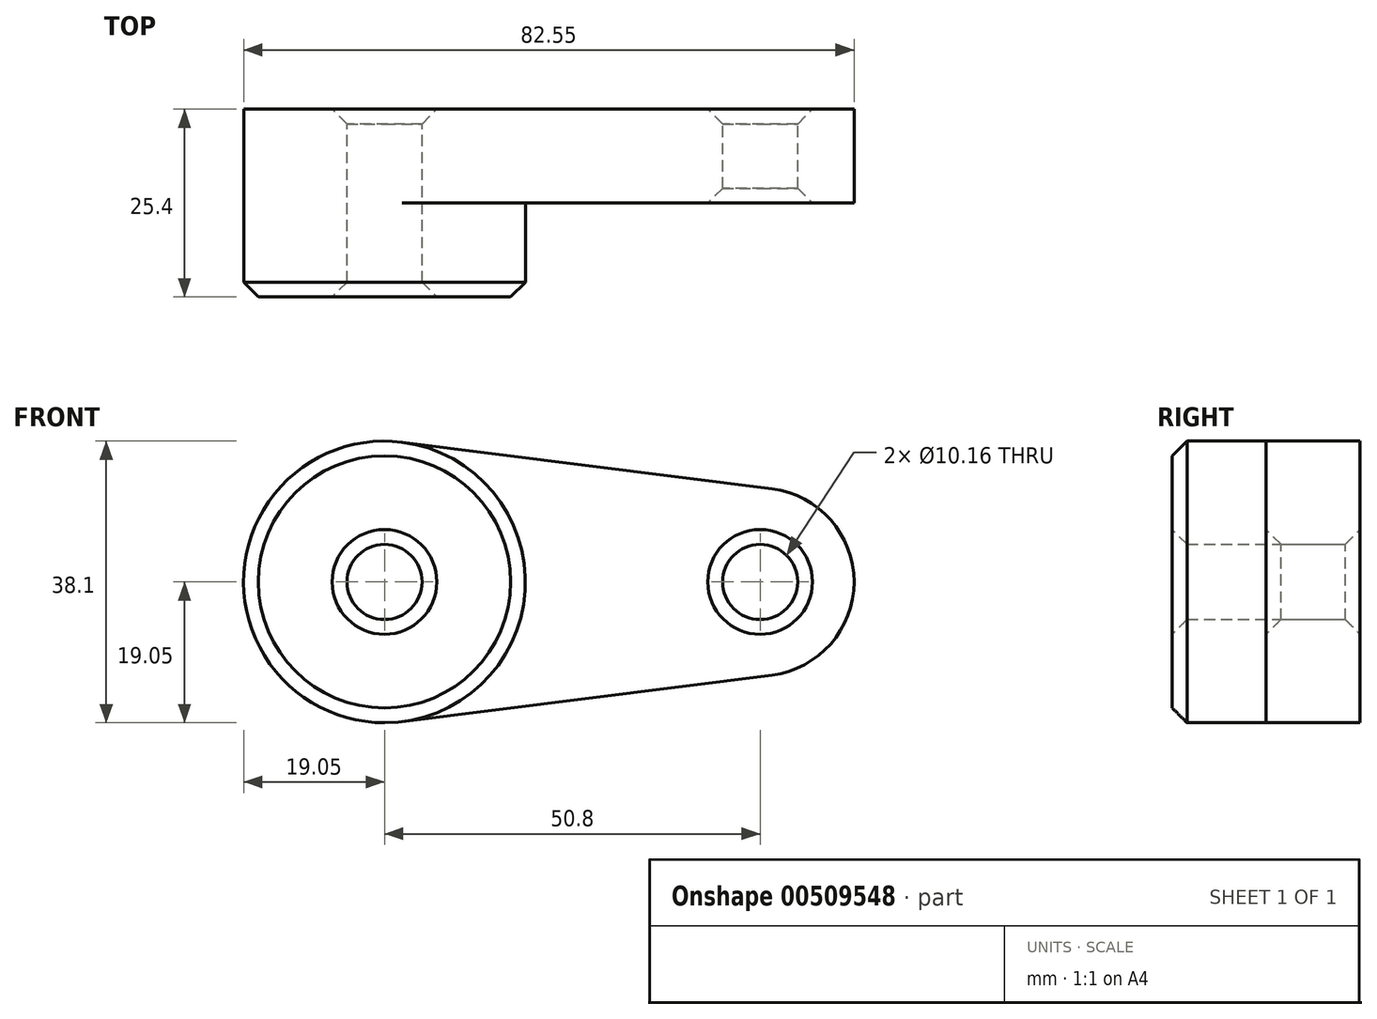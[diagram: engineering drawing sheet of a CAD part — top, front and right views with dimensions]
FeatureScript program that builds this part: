
annotation { "Feature Type Name" : "Feature", "Feature Type Description" : "" }
export const myFeature = defineFeature(function(context is Context, id is Id, definition is map)
    precondition{}
    {
        {
            var Q0;
            Q0=qCreatedBy(makeId("Front.planeOp"),FACE);
            var sketch = newSketch(context, id + "F0", { "sketchPlane" : qUnion([Q0])});
            skCircle(sketch, "E0", {"center": v(0, 0) * mm, "radius": 19.05 * mm});
            skCircle(sketch, "E1", {"center": v(50.8, 0) * mm, "radius": 12.7 * mm});
            skLineSegment(sketch, "E2", {"start": v(2.38, 18.9) * mm, "end": v(52.39, 12.6) * mm});
            skLineSegment(sketch, "E3", {"start": v(2.38, -18.9) * mm, "end": v(52.39, -12.6) * mm});
            skCircle(sketch, "E4", {"center": v(0, 0) * mm, "radius": 5.08 * mm});
            skCircle(sketch, "E5", {"center": v(50.8, 0) * mm, "radius": 5.08 * mm});
            skSolve(sketch);
        }
        {
            var Q0;
            Q0 = qSketchRegion(id + "F0", true);
            extrude(context, id + "F1", {"entities" : qUnion([Q0]), "depth" : 12.7 * mm});
        }
        {
            var Q0;
            Q0=makeQuery(id+"F0.imprint","IMPRINT",FACE,{"disambiguationData":[TD([[makeQuery(id+"F0.imprint","IMPRINT",EDGE,{"derivedFrom":sQuery(id+"F0.wireOp",EDGE,"E4")}),-1.0]])]});
            extrude(context, id + "F2", {"entities" : qUnion([Q0]), "operationType" : NewBodyOperationType.ADD, "depth" : 25.4 * mm});
        }
        {
            var Q0;
            Q0=makeQuery(id+"F2.opExtrude","CAP_EDGE",EDGE,{"disambiguationData":[OSD([sQuery(id+"F0.wireOp",EDGE,"E4")])],"isStart":false});
            var Q1;
            Q1=makeQuery(id+"F2.opExtrude","CAP_EDGE",EDGE,{"disambiguationData":[OSD([sQuery(id+"F0.wireOp",EDGE,"E0")])],"isStart":false});
            var Q2;
            Q2=makeQuery(id+"F1.opExtrude","CAP_EDGE",EDGE,{"disambiguationData":[OSD([sQuery(id+"F0.wireOp",EDGE,"E5")])],"isStart":false});
            var Q3;
            Q3=makeQuery(id+"F1.opExtrude","CAP_EDGE",EDGE,{"disambiguationData":[OSD([sQuery(id+"F0.wireOp",EDGE,"E4")])],"isStart":true});
            var Q4;
            Q4=makeQuery(id+"F1.opExtrude","CAP_EDGE",EDGE,{"disambiguationData":[OSD([sQuery(id+"F0.wireOp",EDGE,"E5")])],"isStart":true});
            chamfer(context, id + "F3", {"entities" : qUnion([Q0, Q1, Q2, Q3, Q4]), "width" : 2 * mm, "tangentPropagation" : true});
        }
    });
